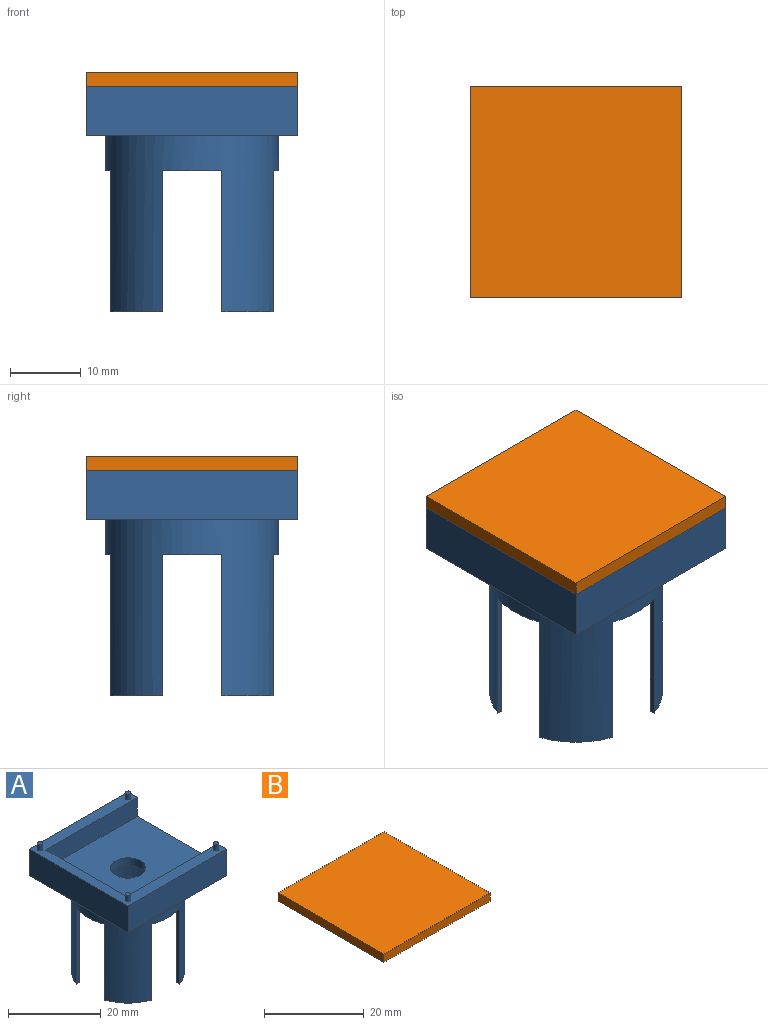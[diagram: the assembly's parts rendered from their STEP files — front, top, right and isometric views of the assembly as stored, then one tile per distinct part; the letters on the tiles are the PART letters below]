
ASSEMBLY  parts=2 mates=1
PART A: 38 faces, bbox 30x30x33.5 mm
  f0: cylinder r=11.5mm len=25mm, axis (0,0,1), area 1119.4mm2, adj f1,f2,f3,f4,f5,f18,f19,f20
  f1: plane 7.29x7.29mm, normal (0,0,-1), area 7.3mm2, adj f0,f17,f24,f27
  f2: plane 7.29x7.29mm, normal (0,0,-1), area 7.3mm2, adj f0,f17,f22,f25
  f3: plane 7.29x7.29mm, normal (0,0,-1), area 7.3mm2, adj f0,f17,f19,f21
  f4: plane 7.29x7.29mm, normal (0,0,-1), area 7.3mm2, adj f0,f17,f18,f28
  f5: plane 23x23mm, normal (0,0,-1), area 369.9mm2, adj f0,f11
  f6: plane 27.75x24.5mm, normal (0,0,1), area 634.3mm2, adj f7,f11,f13,f14,f15
  f7: plane 30x7mm, normal (1,0,0), area 87.5mm2, adj f6,f8,f10,f12,f13,f15,f16
  f8: plane 30x7mm, normal (0,1,0), area 210mm2, adj f7,f9,f12,f16
  f9: plane 30x7mm, normal (-1,0,0), area 210mm2, adj f8,f10,f12,f16
  f10: plane 30x7mm, normal (0,-1,0), area 210mm2, adj f7,f9,f12,f16
  f11: cylinder r=3.81mm len=7.62mm, axis (0,0,1), area 47.9mm2, adj f5,f6
  f12: plane 30x30mm, normal (0,0,-1), area 430.6mm2, adj f7,f8,f9,f10,f17
  f13: plane 27.75x5mm, normal (0,1,0), area 138.7mm2, adj f6,f7,f14,f16
  f14: plane 24.5x5mm, normal (1,0,0), area 122.5mm2, adj f6,f13,f15,f16
  f15: plane 27.75x5mm, normal (0,-1,0), area 138.7mm2, adj f6,f7,f14,f16
  f16: plane 30x30mm, normal (0,0,1), area 215.6mm2, adj f7,f8,f9,f10,f13,f14,f15,f30
  f17: cylinder r=12.22mm len=25mm, axis (0,0,1), area 1235mm2, adj f1,f2,f3,f4,f12,f18,f19,f20
  f18: plane 20x0.77mm, normal (-1,0,0), area 15.5mm2, adj f0,f4,f17,f20
  f19: plane 20x0.77mm, normal (1,0,0), area 15.5mm2, adj f0,f3,f17,f20
  f20: plane 8.39x1.52mm, normal (0,0,-1), area 6.2mm2, adj f0,f17,f18,f19
  f21: plane 20x0.77mm, normal (0,1,0), area 15.5mm2, adj f0,f3,f17,f23
  f22: plane 20x0.77mm, normal (0,-1,0), area 15.5mm2, adj f0,f2,f17,f23
  f23: plane 8.39x1.52mm, normal (0,0,-1), area 6.2mm2, adj f0,f17,f21,f22
  f24: plane 20x0.77mm, normal (-1,0,0), area 15.5mm2, adj f0,f1,f17,f26
  f25: plane 20x0.77mm, normal (1,0,0), area 15.5mm2, adj f0,f2,f17,f26
  f26: plane 8.39x1.52mm, normal (0,0,-1), area 6.2mm2, adj f0,f17,f24,f25
  f27: plane 20x0.77mm, normal (0,-1,0), area 15.5mm2, adj f0,f1,f17,f29
  f28: plane 20x0.77mm, normal (0,1,0), area 15.5mm2, adj f0,f4,f17,f29
  f29: plane 8.39x1.52mm, normal (0,0,-1), area 6.2mm2, adj f0,f17,f27,f28
  f30: cylinder r=0.6mm len=1.5mm, axis (0,0,-1), area 5.7mm2, adj f16,f31
  f31: plane 1.2x1.2mm, normal (0,0,1), area 1.1mm2, adj f30
  f32: cylinder r=0.6mm len=1.5mm, axis (0,0,-1), area 5.7mm2, adj f16,f33
  f33: plane 1.2x1.2mm, normal (0,0,1), area 1.1mm2, adj f32
  f34: cylinder r=0.6mm len=1.5mm, axis (0,0,-1), area 5.7mm2, adj f16,f35
  f35: plane 1.2x1.2mm, normal (0,0,1), area 1.1mm2, adj f34
  f36: cylinder r=0.6mm len=1.5mm, axis (0,0,-1), area 5.7mm2, adj f16,f37
  f37: plane 1.2x1.2mm, normal (0,0,1), area 1.1mm2, adj f36
PART B: 14 faces, bbox 30x30x2 mm
  f0: plane 30x2mm, normal (1,0,0), area 60mm2, adj f1,f3,f4,f5
  f1: plane 30x2mm, normal (0,1,0), area 60mm2, adj f0,f2,f4,f5
  f2: plane 30x2mm, normal (-1,0,0), area 60mm2, adj f1,f3,f4,f5
  f3: plane 30x2mm, normal (0,-1,0), area 60mm2, adj f0,f2,f4,f5
  f4: plane 30x30mm, normal (0,0,1), area 900mm2, adj f0,f1,f2,f3
  f5: plane 30x30mm, normal (0,0,-1), area 895.5mm2, adj f0,f1,f2,f3,f6,f8,f10,f12
  f6: cylinder r=0.6mm len=1.5mm, axis (0,0,-1), area 5.7mm2, adj f5,f7
  f7: plane 1.2x1.2mm, normal (0,0,-1), area 1.1mm2, adj f6
  f8: cylinder r=0.6mm len=1.5mm, axis (0,0,-1), area 5.7mm2, adj f5,f9
  f9: plane 1.2x1.2mm, normal (0,0,-1), area 1.1mm2, adj f8
  f10: cylinder r=0.6mm len=1.5mm, axis (0,0,-1), area 5.7mm2, adj f5,f11
  f11: plane 1.2x1.2mm, normal (0,0,-1), area 1.1mm2, adj f10
  f12: cylinder r=0.6mm len=1.5mm, axis (0,0,-1), area 5.7mm2, adj f5,f13
  f13: plane 1.2x1.2mm, normal (0,0,-1), area 1.1mm2, adj f12
PLACE A at identity
PLACE B t=(0,0,-16.2)mm
MATE fastened B.f8 <-> A.f36  axis (0,0,-1) through (13.4,-13.4,5)mm
